# Revit family: PQHY-P850YSLM-A
name_source: partatom
category: Mechanical Equipment
revit_build: Autodesk Revit Architecture 2012 (Build: 20110916_2132(x64)
units: mm (PartAtom-declared; Revit-internal decimal feet)

## types (6) — shared parameters
Compressor Motor Output (kW) = 22.3
Compressor_Lubricant = MEL32
Compressor_Quantity = 2
Compressor_Type = Inverter scroll hermetic compressor
Cooling Capacity (kW) = 96
Cooling EER (kW/kW) = 5.32
Cooling Power Input (kW) = 18.03
Depth = 550 mm  [stored 1.80446 ft]
External Finish = Galvanized steel sheets
Gas pipe_radius = 21 mm  [stored 0.0688976 ft]
Heat Source unit 1 = PQHY-P450YLM-A
Heat Source unit 1 Breaker size (A) = 40
Heat Source unit 2 = PQHY-P400YLM-A
Heat Source unit 2 Breaker size (A) = 30
Heating COP (kW/kW) = 5.84
Heating Capacity (kW) = 108
Heating Power Input (kW) = 18.49
Height = 1450 mm  [stored 4.75722 ft]
Indoor Unit Model/Quantity = P15 to P250/2 to 50
Indoor Unit Total Capacity = 50 to 130% of heat source unit capacity
Liquid pipe_radius = 10 mm  [stored 0.0328084 ft]
Manufacturer = Mitsubishi Electric Corporation
Maximum Circuit Ampacity (A) = 60.5
Model = PQHY-P850YSLM-A
Note_1 = Refrigerant pipe diameters may change depending on the installation condition. Please refer to the installation manual.
Phase = 3
Protection Devices_Compressor = Over-heat protection
Protection Devices_High pressure (MPa) = High pressure sensor, High pressure switch at 4.15
Protection Devices_Inverter circuit (COMP) = Over-heat protection, Over-current protection
Refrigerant Charge (kg) = 12
Refrigerant type = R410A
Sound Pressure Level (dB(A)) = 56
Space View = Yes
Subcategory = HVAC
URL = http://www.mitsubishielectric.com
Unit Weight (kg) = 434
Water flow rate (m3/h) = 14.4
Width = 1780 mm
zero-valued in all types: Equip_No., SerialNumber, TagNumber

## per-type parameters (varying)
| type | Cooling Current (A) | Cooling Rated Load Ampacity (A) | Heating Current (A) | Heating Rated Load Ampacity (A) | Hertz | Voltage |
| PQHY-P850YSLM-A_380V_50Hz | 30.4 | 29.1 | 31.2 | 30.6 | 50 Hz | 380 V |
| PQHY-P850YSLM-A_380V_60Hz | 30.4 | 29.1 | 31.2 | 30.6 | 60 Hz | 380 V |
| PQHY-P850YSLM-A_400V_50Hz | 28.9 | 27.6 | 29.6 | 29.1 | 50 Hz | 400 V |
| PQHY-P850YSLM-A_400V_60Hz | 28.9 | 27.6 | 29.6 | 29.1 | 60 Hz | 400 V |
| PQHY-P850YSLM-A_415V_50Hz | 27.8 | 26.7 | 28.5 | 28 | 50 Hz | 415 V |
| PQHY-P850YSLM-A_415V_60Hz | 27.8 | 26.7 | 28.5 | 28 | 60 Hz | 415 V |

note: [stored X ft] marks values corroborated as IEEE doubles in the binary element streams (Revit-internal decimal feet)

## geometry (parser evidence)
native form markers: Blend x6, Sweep x4
no freeform markers — native parametric forms only
